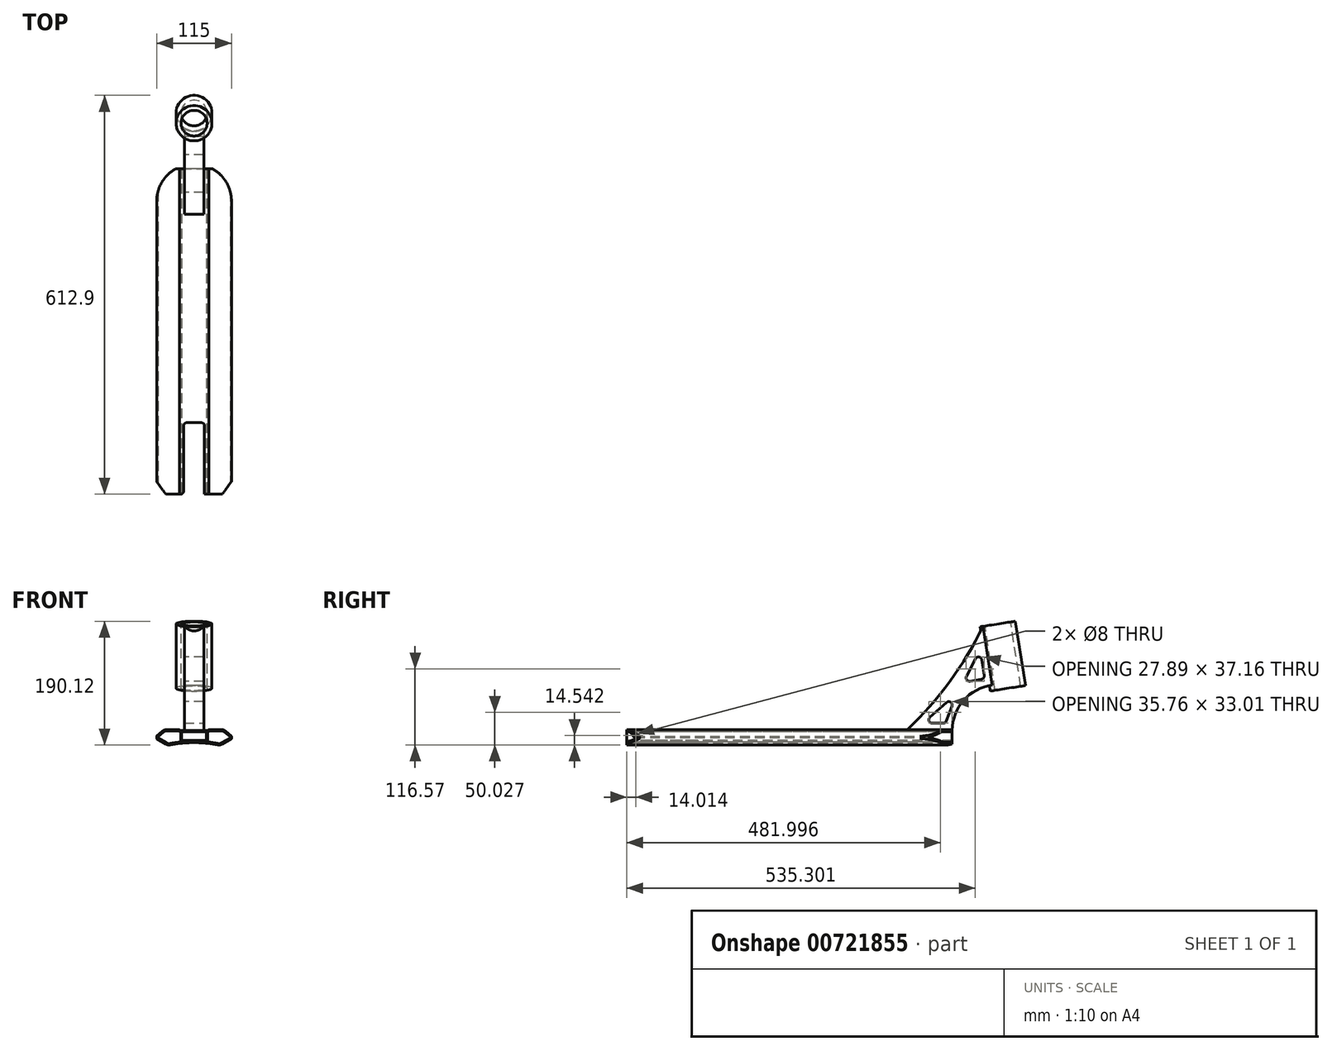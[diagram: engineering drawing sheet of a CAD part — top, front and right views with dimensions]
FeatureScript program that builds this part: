
annotation { "Feature Type Name" : "Feature", "Feature Type Description" : "" }
export const myFeature = defineFeature(function(context is Context, id is Id, definition is map)
    precondition{}
    {
        {
            var Q0;
            Q0=qCreatedBy(makeId("Front.planeOp"),FACE);
            var sketch = newSketch(context, id + "F0", { "sketchPlane" : qUnion([Q0])});
            skLineSegment(sketch, "E0", {"start": v(0, 0) * mm, "end": v(0, 84.74) * mm, "construction": true});
            skLineSegment(sketch, "E1", {"start": v(0, 59.77) * mm, "end": v(22.5, 59.77) * mm});
            skLineSegment(sketch, "E2", {"start": v(22.5, 59.77) * mm, "end": v(22.5, 61.07) * mm});
            skLineSegment(sketch, "E3", {"start": v(22.5, 61.07) * mm, "end": v(45.58, 61.07) * mm});
            skLineSegment(sketch, "E4", {"start": v(45.58, 61.07) * mm, "end": v(57.5, 51.07) * mm});
            skLineSegment(sketch, "E5", {"start": v(57.5, 51.07) * mm, "end": v(57.5, 47.07) * mm});
            skLineSegment(sketch, "E6", {"start": v(57.5, 47.07) * mm, "end": v(40.18, 37.07) * mm});
            skLineSegment(sketch, "E7.MirrorCS", {"start": v(0, 59.77) * mm, "end": v(-22.5, 59.77) * mm});
            skLineSegment(sketch, "E8.MirrorCS", {"start": v(-22.5, 59.77) * mm, "end": v(-22.5, 61.07) * mm});
            skLineSegment(sketch, "E9.MirrorCS", {"start": v(-22.5, 61.07) * mm, "end": v(-45.58, 61.07) * mm});
            skLineSegment(sketch, "E10.MirrorCS", {"start": v(-45.58, 61.07) * mm, "end": v(-57.5, 51.07) * mm});
            skLineSegment(sketch, "E11.MirrorCS", {"start": v(-57.5, 51.07) * mm, "end": v(-57.5, 47.07) * mm});
            skLineSegment(sketch, "E12.MirrorCS", {"start": v(-57.5, 47.07) * mm, "end": v(-40.18, 37.07) * mm});
            skArc(sketch, "E13", {"start": v(40.18, 37.07) * mm, "mid": v(0, 41.15) * mm, "end": v(-40.18, 37.07) * mm});
            skLineSegment(sketch, "E14", {"start": v(-57.5, 47.07) * mm, "end": v(-57.5, 22.93) * mm, "construction": true});
            skSolve(sketch);
        }
        {
            var Q0;
            Q0=makeQuery(id+"F0.imprint","IMPRINT",FACE,{"disambiguationData":[TD([[makeQuery(id+"F0.imprint","IMPRINT",EDGE,{"derivedFrom":sQuery(id+"F0.wireOp",EDGE,"E1")}),-1.0]])]});
            extrude(context, id + "F1", {"entities" : qUnion([Q0]), "endBound" : BoundingType.SYMMETRIC, "depth" : 500 * mm, "offsetDistance" : 25 * mm});
        }
        {
            var Q0;
            Q0=qCreatedBy(makeId("Front.planeOp"),FACE);
            var sketch = newSketch(context, id + "F2", { "sketchPlane" : qUnion([Q0])});
            skLineSegment(sketch, "E15.bottom", {"start": v(-19, 57.77) * mm, "end": v(19, 57.77) * mm});
            skLineSegment(sketch, "E15.top", {"start": v(-19, 44.77) * mm, "end": v(19, 44.77) * mm});
            skLineSegment(sketch, "E15.left", {"start": v(-19, 57.77) * mm, "end": v(-19, 44.77) * mm});
            skLineSegment(sketch, "E15.right", {"start": v(19, 57.77) * mm, "end": v(19, 44.77) * mm});
            skSolve(sketch);
        }
        {
            var Q0;
            Q0 = qSketchRegion(id + "F2", true);
            extrude(context, id + "F3", {"entities" : qUnion([Q0]), "operationType" : NewBodyOperationType.REMOVE, "endBound" : BoundingType.SYMMETRIC, "oppositeDirection" : true, "depth" : 500 * mm, "offsetDistance" : 25 * mm});
        }
        {
            var Q0;
            Q0=makeQuery(id+"F1.opExtrude","SWEPT_EDGE",EDGE,{"disambiguationData":[OSD([sQuery(id+"F0.wireOp",EDGE,"E1"),sQuery(id+"F0.wireOp",EDGE,"E2")])]});
            var Q1;
            Q1=makeQuery(id+"F1.opExtrude","SWEPT_EDGE",EDGE,{"disambiguationData":[OSD([sQuery(id+"F0.wireOp",EDGE,"E7.MirrorCS"),sQuery(id+"F0.wireOp",EDGE,"E8.MirrorCS")])]});
            fillet(context, id + "F4", {"entities" : qUnion([Q0, Q1]), "radius" : 2 * mm, "tangentPropagation" : true, "allowEdgeOverflow" : false});
        }
        {
            var Q0;
            Q0=makeQuery(id+"F1.opExtrude","SWEPT_EDGE",EDGE,{"disambiguationData":[OSD([sQuery(id+"F0.wireOp",EDGE,"E3"),sQuery(id+"F0.wireOp",EDGE,"E4")])]});
            var Q1;
            Q1=makeQuery(id+"F1.opExtrude","SWEPT_EDGE",EDGE,{"disambiguationData":[OSD([sQuery(id+"F0.wireOp",EDGE,"E9.MirrorCS"),sQuery(id+"F0.wireOp",EDGE,"E10.MirrorCS")])]});
            var Q2;
            Q2=makeQuery(id+"F1.opExtrude","SWEPT_EDGE",EDGE,{"disambiguationData":[OSD([sQuery(id+"F0.wireOp",EDGE,"E12.MirrorCS"),sQuery(id+"F0.wireOp",EDGE,"E13")])]});
            var Q3;
            Q3=makeQuery(id+"F1.opExtrude","SWEPT_EDGE",EDGE,{"disambiguationData":[OSD([sQuery(id+"F0.wireOp",EDGE,"E6"),sQuery(id+"F0.wireOp",EDGE,"E13")])]});
            fillet(context, id + "F5", {"entities" : qUnion([Q0, Q1, Q2, Q3]), "radius" : 9 * mm, "tangentPropagation" : true, "allowEdgeOverflow" : false});
        }
        {
            var Q0;
            Q0=makeQuery(id+"F1.opExtrude","SWEPT_EDGE",EDGE,{"disambiguationData":[OSD([sQuery(id+"F0.wireOp",EDGE,"E4"),sQuery(id+"F0.wireOp",EDGE,"E5")])]});
            var Q1;
            Q1=makeQuery(id+"F1.opExtrude","SWEPT_EDGE",EDGE,{"disambiguationData":[OSD([sQuery(id+"F0.wireOp",EDGE,"E5"),sQuery(id+"F0.wireOp",EDGE,"E6")])]});
            var Q2;
            Q2=makeQuery(id+"F1.opExtrude","SWEPT_EDGE",EDGE,{"disambiguationData":[OSD([sQuery(id+"F0.wireOp",EDGE,"E10.MirrorCS"),sQuery(id+"F0.wireOp",EDGE,"E11.MirrorCS")])]});
            var Q3;
            Q3=makeQuery(id+"F1.opExtrude","SWEPT_EDGE",EDGE,{"disambiguationData":[OSD([sQuery(id+"F0.wireOp",EDGE,"E11.MirrorCS"),sQuery(id+"F0.wireOp",EDGE,"E12.MirrorCS")])]});
            fillet(context, id + "F6", {"entities" : qUnion([Q0, Q1, Q2, Q3]), "radius" : 1 * mm, "tangentPropagation" : true, "allowEdgeOverflow" : false});
        }
        {
            var Q0;
            Q0=makeQuery(id+"F1.opExtrude","CAP_FACE",FACE,{"disambiguationData":[OSD([sQuery(id+"F0.wireOp",EDGE,"E1"),sQuery(id+"F0.wireOp",EDGE,"E2"),sQuery(id+"F0.wireOp",EDGE,"E3"),sQuery(id+"F0.wireOp",EDGE,"E4"),sQuery(id+"F0.wireOp",EDGE,"E5"),sQuery(id+"F0.wireOp",EDGE,"E6"),sQuery(id+"F0.wireOp",EDGE,"E7.MirrorCS"),sQuery(id+"F0.wireOp",EDGE,"E8.MirrorCS"),sQuery(id+"F0.wireOp",EDGE,"E9.MirrorCS"),sQuery(id+"F0.wireOp",EDGE,"E10.MirrorCS"),sQuery(id+"F0.wireOp",EDGE,"E11.MirrorCS"),sQuery(id+"F0.wireOp",EDGE,"E12.MirrorCS"),sQuery(id+"F0.wireOp",EDGE,"E13")])],"isStart":false});
            var sketch = newSketch(context, id + "F7", { "sketchPlane" : qUnion([Q0])});
            skLineSegment(sketch, "E16.0.0", {"start": v(43.1, 38.76) * mm, "end": v(57, 46.78) * mm});
            skArc(sketch, "E16.0.1", {"start": v(57, 46.78) * mm, "mid": v(57.37, 47.15) * mm, "end": v(57.5, 47.65) * mm});
            skLineSegment(sketch, "E16.0.2", {"start": v(57.5, 47.65) * mm, "end": v(57.5, 50.6) * mm});
            skArc(sketch, "E16.0.3", {"start": v(57.5, 50.6) * mm, "mid": v(57.4, 51.03) * mm, "end": v(57.14, 51.37) * mm});
            skLineSegment(sketch, "E16.0.4", {"start": v(57.14, 51.37) * mm, "end": v(48.1, 58.96) * mm});
            skArc(sketch, "E16.0.5", {"start": v(48.1, 58.96) * mm, "mid": v(45.38, 60.53) * mm, "end": v(42.3, 61.07) * mm});
            skLineSegment(sketch, "E16.0.6", {"start": v(42.3, 61.07) * mm, "end": v(22.5, 61.07) * mm});
            skArc(sketch, "E16.0.7", {"start": v(22.5, 61.07) * mm, "mid": v(21.77, 60.13) * mm, "end": v(20.63, 59.77) * mm});
            skLineSegment(sketch, "E16.0.8", {"start": v(20.63, 59.77) * mm, "end": v(-20.63, 59.77) * mm});
            skArc(sketch, "E16.0.9", {"start": v(-20.63, 59.77) * mm, "mid": v(-21.77, 60.13) * mm, "end": v(-22.5, 61.07) * mm});
            skLineSegment(sketch, "E16.0.10", {"start": v(-22.5, 61.07) * mm, "end": v(-42.3, 61.07) * mm});
            skArc(sketch, "E16.0.11", {"start": v(-42.3, 61.07) * mm, "mid": v(-45.38, 60.53) * mm, "end": v(-48.1, 58.96) * mm});
            skLineSegment(sketch, "E16.0.12", {"start": v(-48.1, 58.96) * mm, "end": v(-57.14, 51.37) * mm});
            skArc(sketch, "E16.0.13", {"start": v(-57.14, 51.37) * mm, "mid": v(-57.4, 51.03) * mm, "end": v(-57.5, 50.6) * mm});
            skLineSegment(sketch, "E16.0.14", {"start": v(-57.5, 50.6) * mm, "end": v(-57.5, 47.65) * mm});
            skArc(sketch, "E16.0.15", {"start": v(-57.5, 47.65) * mm, "mid": v(-57.37, 47.15) * mm, "end": v(-57, 46.78) * mm});
            skLineSegment(sketch, "E16.0.16", {"start": v(-57, 46.78) * mm, "end": v(-43.1, 38.76) * mm});
            skArc(sketch, "E16.0.17", {"start": v(-43.1, 38.76) * mm, "mid": v(-40.12, 37.68) * mm, "end": v(-36.94, 37.7) * mm});
            skArc(sketch, "E16.0.18", {"start": v(-36.94, 37.7) * mm, "mid": v(0, 41.15) * mm, "end": v(36.94, 37.7) * mm});
            skArc(sketch, "E16.0.19", {"start": v(36.94, 37.7) * mm, "mid": v(40.12, 37.68) * mm, "end": v(43.1, 38.76) * mm});
            skArc(sketch, "E17.0", {"start": v(37.3, 39.67) * mm, "mid": v(39.78, 39.65) * mm, "end": v(42.1, 40.5) * mm});
            skArc(sketch, "E17.1", {"start": v(-37.3, 39.67) * mm, "mid": v(0, 43.15) * mm, "end": v(37.3, 39.67) * mm});
            skArc(sketch, "E17.2", {"start": v(-42.1, 40.5) * mm, "mid": v(-39.78, 39.65) * mm, "end": v(-37.3, 39.67) * mm});
            skLineSegment(sketch, "E17.3", {"start": v(-55.5, 48.23) * mm, "end": v(-42.1, 40.5) * mm});
            skLineSegment(sketch, "E17.4", {"start": v(-55.5, 50.14) * mm, "end": v(-55.5, 48.23) * mm});
            skLineSegment(sketch, "E17.5", {"start": v(42.3, 59.07) * mm, "end": v(23.58, 59.07) * mm});
            skArc(sketch, "E17.6", {"start": v(46.8, 57.43) * mm, "mid": v(44.7, 58.65) * mm, "end": v(42.3, 59.07) * mm});
            skLineSegment(sketch, "E17.7", {"start": v(55.5, 50.14) * mm, "end": v(46.8, 57.43) * mm});
            skLineSegment(sketch, "E17.8", {"start": v(55.5, 48.23) * mm, "end": v(55.5, 50.14) * mm});
            skArc(sketch, "E17.9", {"start": v(23.58, 59.07) * mm, "mid": v(22.24, 58.1) * mm, "end": v(20.63, 57.77) * mm});
            skLineSegment(sketch, "E17.10", {"start": v(20.63, 57.77) * mm, "end": v(-20.63, 57.77) * mm});
            skArc(sketch, "E17.11", {"start": v(-20.63, 57.77) * mm, "mid": v(-22.24, 58.1) * mm, "end": v(-23.58, 59.07) * mm});
            skLineSegment(sketch, "E17.12", {"start": v(-23.58, 59.07) * mm, "end": v(-42.3, 59.07) * mm});
            skArc(sketch, "E17.13", {"start": v(-42.3, 59.07) * mm, "mid": v(-44.7, 58.65) * mm, "end": v(-46.8, 57.43) * mm});
            skLineSegment(sketch, "E17.14", {"start": v(42.1, 40.5) * mm, "end": v(55.5, 48.23) * mm});
            skLineSegment(sketch, "E17.15", {"start": v(-46.8, 57.43) * mm, "end": v(-55.5, 50.14) * mm});
            skLineSegment(sketch, "E18", {"start": v(-20.63, 57.77) * mm, "end": v(-20.63, 42.1) * mm});
            skLineSegment(sketch, "E19", {"start": v(20.63, 57.77) * mm, "end": v(20.63, 42.1) * mm});
            skSolve(sketch);
        }
        {
            var Q0;
            {var subQ1=sQuery(id+"F7.wireOp",EDGE,"E17.0");Q0=makeQuery(id+"F7.imprint","IMPRINT",FACE,{"disambiguationData":[TD([[makeQuery(id+"F7.imprint","IMPRINT",EDGE,{"derivedFrom":subQ1}),1.0]])]});}
            var Q1;
            {var subQ0=sQuery(id+"F7.wireOp",EDGE,"E17.2");Q1=makeQuery(id+"F7.imprint","IMPRINT",FACE,{"disambiguationData":[TD([[makeQuery(id+"F7.imprint","IMPRINT",EDGE,{"derivedFrom":subQ0}),1.0]])]});}
            extrude(context, id + "F8", {"entities" : qUnion([Q0, Q1]), "operationType" : NewBodyOperationType.REMOVE, "oppositeDirection" : true, "depth" : 505 * mm, "offsetDistance" : 25 * mm});
        }
        {
            var Q0;
            Q0=qCreatedBy(makeId("Top.planeOp"),FACE);
            var sketch = newSketch(context, id + "F9", { "sketchPlane" : qUnion([Q0])});
            skArc(sketch, "E20", {"start": v(57.5, 200) * mm, "mid": v(0, 257.5) * mm, "end": v(-57.5, 200) * mm});
            skLineSegment(sketch, "E21", {"start": v(0, 0) * mm, "end": v(0, 250) * mm});
            skLineSegment(sketch, "E22", {"start": v(0, 200) * mm, "end": v(-57.5, 200) * mm});
            skLineSegment(sketch, "E23", {"start": v(0, 200) * mm, "end": v(57.5, 200) * mm});
            skLineSegment(sketch, "E24", {"start": v(-57.5, 200) * mm, "end": v(-57.5, 280) * mm});
            skLineSegment(sketch, "E25", {"start": v(57.5, 200) * mm, "end": v(57.5, 280) * mm});
            skLineSegment(sketch, "E26", {"start": v(57.5, 280) * mm, "end": v(-57.5, 280) * mm});
            skSolve(sketch);
        }
        {
            var Q0;
            Q0=makeQuery(id+"F9.imprint","IMPRINT",FACE,{"disambiguationData":[TD([[makeQuery(id+"F9.imprint","IMPRINT",EDGE,{"derivedFrom":sQuery(id+"F9.wireOp",EDGE,"E20")}),-1.0]])]});
            extrude(context, id + "F10", {"entities" : qUnion([Q0]), "operationType" : NewBodyOperationType.REMOVE, "depth" : 118.9 * mm, "offsetDistance" : 25 * mm, "hasSecondDirection" : true, "secondDirectionBound" : SecondDirectionBoundingType.THROUGH_ALL, "secondDirectionOppositeDirection" : true, "secondDirectionDepth" : 25 * mm});
        }
        {
            var Q0;
            Q0=qCreatedBy(makeId("Top.planeOp"),FACE);
            var sketch = newSketch(context, id + "F11", { "sketchPlane" : qUnion([Q0])});
            skLineSegment(sketch, "E27", {"start": v(68, -346) * mm, "end": v(68, -216) * mm});
            skLineSegment(sketch, "E28", {"start": v(16, -250) * mm, "end": v(16, -140) * mm});
            skLineSegment(sketch, "E29", {"start": v(16, -250) * mm, "end": v(43.3, -250) * mm});
            skLineSegment(sketch, "E30", {"start": v(43.3, -250) * mm, "end": v(68, -216) * mm});
            skLineSegment(sketch, "E31.MirrorCS", {"start": v(-68, -346) * mm, "end": v(-68, -216) * mm});
            skLineSegment(sketch, "E32.MirrorCS", {"start": v(-43.3, -250) * mm, "end": v(-68, -216) * mm});
            skLineSegment(sketch, "E33.MirrorCS", {"start": v(-16, -250) * mm, "end": v(-43.3, -250) * mm});
            skLineSegment(sketch, "E34.MirrorCS", {"start": v(-16, -250) * mm, "end": v(-16, -140) * mm});
            skLineSegment(sketch, "E35", {"start": v(0, -346) * mm, "end": v(0, 0) * mm, "construction": true});
            skLineSegment(sketch, "E36", {"start": v(-16, -140) * mm, "end": v(16, -140) * mm});
            skLineSegment(sketch, "E37", {"start": v(68, -346) * mm, "end": v(-68, -346) * mm});
            skSolve(sketch);
        }
        {
            var Q0;
            Q0=makeQuery(id+"F11.imprint","IMPRINT",FACE,{"disambiguationData":[TD([[makeQuery(id+"F11.imprint","IMPRINT",EDGE,{"derivedFrom":sQuery(id+"F11.wireOp",EDGE,"E27")}),1.0]])]});
            extrude(context, id + "F12", {"entities" : qUnion([Q0]), "operationType" : NewBodyOperationType.REMOVE, "oppositeDirection" : true, "depth" : 25 * mm, "offsetDistance" : 25 * mm, "hasSecondDirection" : true, "secondDirectionBound" : SecondDirectionBoundingType.THROUGH_ALL, "secondDirectionOppositeDirection" : false, "secondDirectionDepth" : 25 * mm});
        }
        {
            var Q0;
            {var subQ2=sQuery(id+"F11.wireOp",EDGE,"E34.MirrorCS");Q0=makeQuery(id+"F12.boolean.opBoolean","COPY",EDGE,{"disambiguationData":[TD([makeQuery(id+"F3.boolean.opBoolean","COPY",FACE,{"derivedFrom":makeQuery(id+"F3.opExtrude","SWEPT_FACE",FACE,{"disambiguationData":[OSD([sQuery(id+"F2.wireOp",EDGE,"E15.bottom")])]})})])],"derivedFrom":makeQuery(id+"F12.opExtrude","SWEPT_EDGE",EDGE,{"disambiguationData":[OSD([sQuery(id+"F11.wireOp",EDGE,"E33.MirrorCS"),subQ2])]})});}
            var Q1;
            {var subQ0=sQuery(id+"F11.wireOp",EDGE,"E36");var subQ1=sQuery(id+"F11.wireOp",EDGE,"E34.MirrorCS");Q1=makeQuery(id+"F12.boolean.opBoolean","COPY",EDGE,{"disambiguationData":[TD([makeQuery(id+"F3.boolean.opBoolean","COPY",FACE,{"derivedFrom":makeQuery(id+"F3.opExtrude","SWEPT_FACE",FACE,{"disambiguationData":[OSD([sQuery(id+"F2.wireOp",EDGE,"E15.bottom")])]})})])],"derivedFrom":makeQuery(id+"F12.opExtrude","SWEPT_EDGE",EDGE,{"disambiguationData":[OSD([subQ1,subQ0])]})});}
            var Q2;
            {var subQ0=sQuery(id+"F11.wireOp",EDGE,"E28");var subQ1=sQuery(id+"F11.wireOp",EDGE,"E36");Q2=makeQuery(id+"F12.boolean.opBoolean","COPY",EDGE,{"disambiguationData":[TD([makeQuery(id+"F3.boolean.opBoolean","COPY",FACE,{"derivedFrom":makeQuery(id+"F3.opExtrude","SWEPT_FACE",FACE,{"disambiguationData":[OSD([sQuery(id+"F2.wireOp",EDGE,"E15.bottom")])]})})])],"derivedFrom":makeQuery(id+"F12.opExtrude","SWEPT_EDGE",EDGE,{"disambiguationData":[OSD([subQ0,subQ1])]})});}
            var Q3;
            {var subQ2=sQuery(id+"F11.wireOp",EDGE,"E28");Q3=makeQuery(id+"F12.boolean.opBoolean","COPY",EDGE,{"disambiguationData":[TD([makeQuery(id+"F3.boolean.opBoolean","COPY",FACE,{"derivedFrom":makeQuery(id+"F3.opExtrude","SWEPT_FACE",FACE,{"disambiguationData":[OSD([sQuery(id+"F2.wireOp",EDGE,"E15.bottom")])]})})])],"derivedFrom":makeQuery(id+"F12.opExtrude","SWEPT_EDGE",EDGE,{"disambiguationData":[OSD([subQ2,sQuery(id+"F11.wireOp",EDGE,"E29")])]})});}
            var Q4;
            {var subQ0=sQuery(id+"F11.wireOp",EDGE,"E34.MirrorCS");var subQ1=sQuery(id+"F11.wireOp",EDGE,"E36");Q4=makeQuery(id+"F12.boolean.opBoolean","COPY",EDGE,{"disambiguationData":[TD([makeQuery(id+"F1.opExtrude","SWEPT_FACE",FACE,{"disambiguationData":[OSD([sQuery(id+"F0.wireOp",EDGE,"E13")])]})])],"derivedFrom":makeQuery(id+"F12.opExtrude","SWEPT_EDGE",EDGE,{"disambiguationData":[OSD([subQ0,subQ1])]})});}
            var Q5;
            {var subQ0=sQuery(id+"F11.wireOp",EDGE,"E28");var subQ1=sQuery(id+"F11.wireOp",EDGE,"E36");Q5=makeQuery(id+"F12.boolean.opBoolean","COPY",EDGE,{"disambiguationData":[TD([makeQuery(id+"F1.opExtrude","SWEPT_FACE",FACE,{"disambiguationData":[OSD([sQuery(id+"F0.wireOp",EDGE,"E13")])]})])],"derivedFrom":makeQuery(id+"F12.opExtrude","SWEPT_EDGE",EDGE,{"disambiguationData":[OSD([subQ0,subQ1])]})});}
            fillet(context, id + "F13", {"entities" : qUnion([Q0, Q1, Q2, Q3, Q4, Q5]), "radius" : 5 * mm, "tangentPropagation" : true, "allowEdgeOverflow" : false});
        }
        {
            var Q0;
            Q0=makeQuery(id+"F8.boolean.opBoolean","COPY",FACE,{"derivedFrom":makeQuery(id+"F8.opExtrude","SWEPT_FACE",FACE,{"disambiguationData":[OSD([sQuery(id+"F7.wireOp",EDGE,"E19")])]})});
            var sketch = newSketch(context, id + "F14", { "sketchPlane" : qUnion([Q0])});
            skPoint(sketch, "E38", {"position": v(-235.99, 52.1) * mm});
            skSolve(sketch);
        }
        {
            var Q0;
            Q0=sQuery(id+"F14.wireOp",VERTEX,"E38");
            var Q1;
            Q1=makeQuery(id+"F1.opExtrude","SWEPT_BODY",BODY,{"disambiguationData":[OSD([sQuery(id+"F0.wireOp",EDGE,"E1"),sQuery(id+"F0.wireOp",EDGE,"E2"),sQuery(id+"F0.wireOp",EDGE,"E3"),sQuery(id+"F0.wireOp",EDGE,"E4"),sQuery(id+"F0.wireOp",EDGE,"E5"),sQuery(id+"F0.wireOp",EDGE,"E6"),sQuery(id+"F0.wireOp",EDGE,"E7.MirrorCS"),sQuery(id+"F0.wireOp",EDGE,"E8.MirrorCS"),sQuery(id+"F0.wireOp",EDGE,"E9.MirrorCS"),sQuery(id+"F0.wireOp",EDGE,"E10.MirrorCS"),sQuery(id+"F0.wireOp",EDGE,"E11.MirrorCS"),sQuery(id+"F0.wireOp",EDGE,"E12.MirrorCS"),sQuery(id+"F0.wireOp",EDGE,"E13")])]});
            hole(context, id + "F15", {"style" : HoleStyle.SIMPLE, "endStyle" : HoleEndStyle.BLIND, "holeDiameter" : 8 * mm, "majorDiameter" : 5 * mm, "holeDepth" : 50 * mm, "isTappedThrough" : true, "tappedDepth" : 12 * mm, "tapClearance" : 3, "locations" : qUnion([Q0]), "scope" : qUnion([Q1])});
        }
        {
            var Q0;
            Q0=qCreatedBy(makeId("Right.planeOp"),FACE);
            var sketch = newSketch(context, id + "F16", { "sketchPlane" : qUnion([Q0])});
            skLineSegment(sketch, "E39", {"start": v(180, 59.77) * mm, "end": v(250, 59.77) * mm});
            skArc(sketch, "E40", {"start": v(311.71, 129.28) * mm, "mid": v(267.66, 106.25) * mm, "end": v(250, 59.77) * mm});
            skLineSegment(sketch, "E41", {"start": v(311.71, 129.28) * mm, "end": v(313.03, 121) * mm});
            skLineSegment(sketch, "E42", {"start": v(313.03, 121) * mm, "end": v(358.46, 128.2) * mm});
            skLineSegment(sketch, "E43", {"start": v(358.46, 128.2) * mm, "end": v(342.82, 226.97) * mm});
            skLineSegment(sketch, "E44", {"start": v(342.82, 226.97) * mm, "end": v(297.38, 219.77) * mm});
            skArc(sketch, "E45", {"start": v(180, 59.77) * mm, "mid": v(245.97, 134.43) * mm, "end": v(297.38, 219.77) * mm});
            skSolve(sketch);
        }
        {
            var Q0;
            Q0=makeQuery(id+"F16.imprint","IMPRINT",FACE,{"disambiguationData":[TD([[makeQuery(id+"F16.imprint","IMPRINT",EDGE,{"derivedFrom":sQuery(id+"F16.wireOp",EDGE,"E39")}),1.0]])]});
            extrude(context, id + "F17", {"entities" : qUnion([Q0]), "operationType" : NewBodyOperationType.ADD, "endBound" : BoundingType.SYMMETRIC, "depth" : 30 * mm, "offsetDistance" : 25 * mm});
        }
        {
            var Q0;
            Q0=makeQuery(id+"F17.opExtrude","SWEPT_FACE",FACE,{"disambiguationData":[OSD([sQuery(id+"F16.wireOp",EDGE,"E44")])]});
            var sketch = newSketch(context, id + "F18", { "sketchPlane" : qUnion([Q0])});
            skCircle(sketch, "E46", {"center": v(0, 351.1) * mm, "radius": 27.5 * mm});
            skSolve(sketch);
        }
        {
            var Q0;
            Q0 = qSketchRegion(id + "F18", true);
            extrude(context, id + "F19", {"entities" : qUnion([Q0]), "operationType" : NewBodyOperationType.ADD, "oppositeDirection" : true, "depth" : 100 * mm, "offsetDistance" : 25 * mm});
        }
        {
            var Q0;
            Q0=makeQuery(id+"F19.boolean.opBoolean","MERGE",FACE,{"derivedFrom":[makeQuery(id+"F17.opExtrude","SWEPT_FACE",FACE,{"disambiguationData":[OSD([sQuery(id+"F16.wireOp",EDGE,"E44")])]}),makeQuery(id+"F19.opExtrude","CAP_FACE",FACE,{"disambiguationData":[OSD([sQuery(id+"F18.wireOp",EDGE,"E46")])],"isStart":true})]});
            var sketch = newSketch(context, id + "F20", { "sketchPlane" : qUnion([Q0])});
            skPoint(sketch, "E47", {"position": v(0, 351.1) * mm});
            skSolve(sketch);
        }
        {
            var Q0;
            Q0=sQuery(id+"F20.wireOp",VERTEX,"E47");
            var Q1;
            Q1=makeQuery(id+"F1.opExtrude","SWEPT_BODY",BODY,{"disambiguationData":[OSD([sQuery(id+"F0.wireOp",EDGE,"E1"),sQuery(id+"F0.wireOp",EDGE,"E2"),sQuery(id+"F0.wireOp",EDGE,"E3"),sQuery(id+"F0.wireOp",EDGE,"E4"),sQuery(id+"F0.wireOp",EDGE,"E5"),sQuery(id+"F0.wireOp",EDGE,"E6"),sQuery(id+"F0.wireOp",EDGE,"E7.MirrorCS"),sQuery(id+"F0.wireOp",EDGE,"E8.MirrorCS"),sQuery(id+"F0.wireOp",EDGE,"E9.MirrorCS"),sQuery(id+"F0.wireOp",EDGE,"E10.MirrorCS"),sQuery(id+"F0.wireOp",EDGE,"E11.MirrorCS"),sQuery(id+"F0.wireOp",EDGE,"E12.MirrorCS"),sQuery(id+"F0.wireOp",EDGE,"E13")])]});
            hole(context, id + "F21", {"style" : HoleStyle.SIMPLE, "endStyle" : HoleEndStyle.THROUGH, "holeDiameter" : 40 * mm, "majorDiameter" : 5 * mm, "isTappedThrough" : true, "tappedDepth" : 12 * mm, "tapClearance" : 3, "locations" : qUnion([Q0]), "scope" : qUnion([Q1])});
        }
        {
            var Q0;
            Q0=makeQuery(id+"F17.opExtrude","CAP_FACE",FACE,{"disambiguationData":[OSD([sQuery(id+"F16.wireOp",EDGE,"E39"),sQuery(id+"F16.wireOp",EDGE,"E40"),sQuery(id+"F16.wireOp",EDGE,"E41"),sQuery(id+"F16.wireOp",EDGE,"E42"),sQuery(id+"F16.wireOp",EDGE,"E43"),sQuery(id+"F16.wireOp",EDGE,"E44"),sQuery(id+"F16.wireOp",EDGE,"E45")])],"isStart":false});
            var sketch = newSketch(context, id + "F22", { "sketchPlane" : qUnion([Q0])});
            skLineSegment(sketch, "E48", {"start": v(206, 71.07) * mm, "end": v(240, 71.07) * mm});
            skLineSegment(sketch, "E49", {"start": v(240, 71.07) * mm, "end": v(256.38, 116.07) * mm});
            skLineSegment(sketch, "E50", {"start": v(256.38, 116.07) * mm, "end": v(206, 71.07) * mm});
            skLineSegment(sketch, "E51", {"start": v(267.38, 134.02) * mm, "end": v(299.97, 139.18) * mm});
            skLineSegment(sketch, "E52", {"start": v(299.97, 139.18) * mm, "end": v(292.93, 183.63) * mm});
            skLineSegment(sketch, "E53", {"start": v(292.93, 183.63) * mm, "end": v(267.38, 134.02) * mm});
            skSolve(sketch);
        }
        {
            var Q0;
            Q0=makeQuery(id+"F22.imprint","IMPRINT",FACE,{"disambiguationData":[TD([[makeQuery(id+"F22.imprint","IMPRINT",EDGE,{"derivedFrom":sQuery(id+"F22.wireOp",EDGE,"E51")}),1.0]])]});
            var Q1;
            Q1=makeQuery(id+"F22.imprint","IMPRINT",FACE,{"disambiguationData":[TD([[makeQuery(id+"F22.imprint","IMPRINT",EDGE,{"derivedFrom":sQuery(id+"F22.wireOp",EDGE,"E48")}),1.0]])]});
            extrude(context, id + "F23", {"entities" : qUnion([Q0, Q1]), "operationType" : NewBodyOperationType.REMOVE, "endBound" : BoundingType.THROUGH_ALL, "oppositeDirection" : true, "depth" : 25 * mm, "offsetDistance" : 25 * mm});
        }
        {
            var Q0;
            Q0=makeQuery(id+"F23.boolean.opBoolean","COPY",EDGE,{"derivedFrom":makeQuery(id+"F23.opExtrude","SWEPT_EDGE",EDGE,{"disambiguationData":[OSD([sQuery(id+"F22.wireOp",EDGE,"E51"),sQuery(id+"F22.wireOp",EDGE,"E52")])]})});
            var Q1;
            Q1=makeQuery(id+"F23.boolean.opBoolean","COPY",EDGE,{"derivedFrom":makeQuery(id+"F23.opExtrude","SWEPT_EDGE",EDGE,{"disambiguationData":[OSD([sQuery(id+"F22.wireOp",EDGE,"E52"),sQuery(id+"F22.wireOp",EDGE,"E53")])]})});
            var Q2;
            Q2=makeQuery(id+"F23.boolean.opBoolean","COPY",EDGE,{"derivedFrom":makeQuery(id+"F23.opExtrude","SWEPT_EDGE",EDGE,{"disambiguationData":[OSD([sQuery(id+"F22.wireOp",EDGE,"E51"),sQuery(id+"F22.wireOp",EDGE,"E53")])]})});
            var Q3;
            Q3=makeQuery(id+"F23.boolean.opBoolean","COPY",EDGE,{"derivedFrom":makeQuery(id+"F23.opExtrude","SWEPT_EDGE",EDGE,{"disambiguationData":[OSD([sQuery(id+"F22.wireOp",EDGE,"E48"),sQuery(id+"F22.wireOp",EDGE,"E50")])]})});
            var Q4;
            Q4=makeQuery(id+"F23.boolean.opBoolean","COPY",EDGE,{"derivedFrom":makeQuery(id+"F23.opExtrude","SWEPT_EDGE",EDGE,{"disambiguationData":[OSD([sQuery(id+"F22.wireOp",EDGE,"E48"),sQuery(id+"F22.wireOp",EDGE,"E49")])]})});
            var Q5;
            Q5=makeQuery(id+"F23.boolean.opBoolean","COPY",EDGE,{"derivedFrom":makeQuery(id+"F23.opExtrude","SWEPT_EDGE",EDGE,{"disambiguationData":[OSD([sQuery(id+"F22.wireOp",EDGE,"E49"),sQuery(id+"F22.wireOp",EDGE,"E50")])]})});
            fillet(context, id + "F24", {"entities" : qUnion([Q0, Q1, Q2, Q3, Q4, Q5]), "radius" : 5 * mm, "tangentPropagation" : true, "allowEdgeOverflow" : false});
        }
    });
